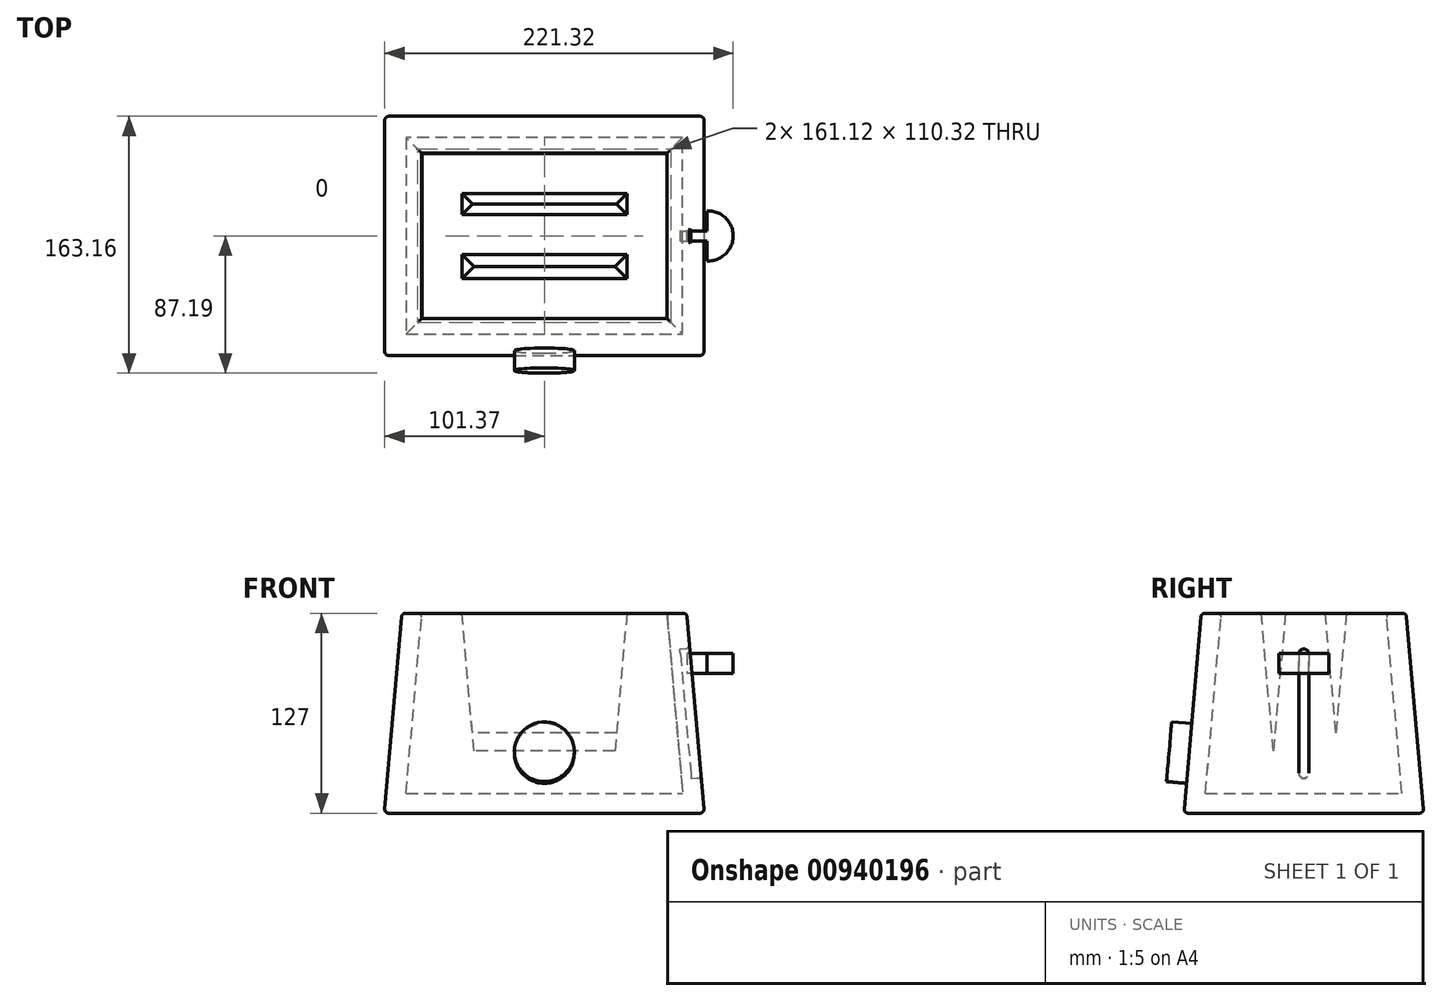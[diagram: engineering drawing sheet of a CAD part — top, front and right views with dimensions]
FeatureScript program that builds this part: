
annotation { "Feature Type Name" : "Feature", "Feature Type Description" : "" }
export const myFeature = defineFeature(function(context is Context, id is Id, definition is map)
    precondition{}
    {
        {
            var Q0;
            Q0=qCreatedBy(makeId("Top.planeOp"),FACE);
            var sketch = newSketch(context, id + "F0", { "sketchPlane" : qUnion([Q0])});
            skLineSegment(sketch, "E0.bottom", {"start": v(101.6, -76.2) * mm, "end": v(-101.6, -76.2) * mm});
            skLineSegment(sketch, "E0.top", {"start": v(101.6, 76.2) * mm, "end": v(-101.6, 76.2) * mm});
            skLineSegment(sketch, "E0.left", {"start": v(101.6, -76.2) * mm, "end": v(101.6, 76.2) * mm});
            skLineSegment(sketch, "E0.right", {"start": v(-101.6, -76.2) * mm, "end": v(-101.6, 76.2) * mm});
            skPoint(sketch, "E0.middle", {"position": v(0, 0) * mm});
            skSolve(sketch);
        }
        {
            var Q0;
            Q0 = qSketchRegion(id + "F0", true);
            extrude(context, id + "F1", {"entities" : qUnion([Q0]), "depth" : 127 * mm, "offsetDistance" : 25.4 * mm, "hasDraft" : true, "draftAngle" : 5 * degree, "draftPullDirection" : true});
        }
        {
            var Q0;
            Q0=makeQuery(id+"F1.opExtrude","CAP_FACE",FACE,{"disambiguationData":[OSD([sQuery(id+"F0.wireOp",EDGE,"E0.bottom"),sQuery(id+"F0.wireOp",EDGE,"E0.top"),sQuery(id+"F0.wireOp",EDGE,"E0.left"),sQuery(id+"F0.wireOp",EDGE,"E0.right")])],"isStart":false});
            var sketch = newSketch(context, id + "F2", { "sketchPlane" : qUnion([Q0])});
            skLineSegment(sketch, "E1.bottom", {"start": v(77.79, -52.39) * mm, "end": v(-77.79, -52.39) * mm});
            skLineSegment(sketch, "E1.top", {"start": v(77.79, 52.39) * mm, "end": v(-77.79, 52.39) * mm});
            skLineSegment(sketch, "E1.left", {"start": v(77.79, -52.39) * mm, "end": v(77.79, 52.39) * mm});
            skLineSegment(sketch, "E1.right", {"start": v(-77.79, -52.39) * mm, "end": v(-77.79, 52.39) * mm});
            skPoint(sketch, "E1.middle", {"position": v(0, 0) * mm});
            skSolve(sketch);
        }
        {
            var Q0;
            Q0=makeQuery(id+"F2.imprint","IMPRINT",FACE,{"disambiguationData":[TD([[makeQuery(id+"F2.imprint","IMPRINT",EDGE,{"derivedFrom":sQuery(id+"F2.wireOp",EDGE,"E1.bottom")}),-1.0]])]});
            extrude(context, id + "F3", {"entities" : qUnion([Q0]), "operationType" : NewBodyOperationType.REMOVE, "oppositeDirection" : true, "depth" : 114.3 * mm, "offsetDistance" : 25.4 * mm, "hasDraft" : true, "draftAngle" : 5 * degree});
        }
        {
            var Q0;
            Q0=makeQuery(id+"F1.opExtrude","CAP_FACE",FACE,{"disambiguationData":[OSD([sQuery(id+"F0.wireOp",EDGE,"E0.bottom"),sQuery(id+"F0.wireOp",EDGE,"E0.top"),sQuery(id+"F0.wireOp",EDGE,"E0.left"),sQuery(id+"F0.wireOp",EDGE,"E0.right")])],"isStart":false});
            var sketch = newSketch(context, id + "F4", { "sketchPlane" : qUnion([Q0])});
            skLineSegment(sketch, "E2.bottom", {"start": v(77.79, -52.39) * mm, "end": v(-77.79, -52.39) * mm});
            skLineSegment(sketch, "E2.top", {"start": v(77.79, 52.39) * mm, "end": v(-77.79, 52.39) * mm});
            skLineSegment(sketch, "E2.left", {"start": v(77.79, -52.39) * mm, "end": v(77.79, 52.39) * mm});
            skLineSegment(sketch, "E2.right", {"start": v(-77.79, -52.39) * mm, "end": v(-77.79, 52.39) * mm});
            skPoint(sketch, "E2.middle", {"position": v(0, 0) * mm});
            skLineSegment(sketch, "E3.bottom", {"start": v(52.39, 13.71) * mm, "end": v(-52.39, 13.71) * mm});
            skLineSegment(sketch, "E3.top", {"start": v(52.39, 26.99) * mm, "end": v(-52.39, 26.99) * mm});
            skLineSegment(sketch, "E3.left", {"start": v(52.39, 13.71) * mm, "end": v(52.39, 26.99) * mm});
            skLineSegment(sketch, "E3.right", {"start": v(-52.39, 13.71) * mm, "end": v(-52.39, 26.99) * mm});
            skPoint(sketch, "E3.middle", {"position": v(0, 20.35) * mm});
            skLineSegment(sketch, "E4.bottom", {"start": v(52.39, -26.99) * mm, "end": v(-52.39, -26.99) * mm});
            skLineSegment(sketch, "E4.top", {"start": v(52.39, -11.69) * mm, "end": v(-52.39, -11.69) * mm});
            skLineSegment(sketch, "E4.left", {"start": v(52.39, -26.99) * mm, "end": v(52.39, -11.69) * mm});
            skLineSegment(sketch, "E4.right", {"start": v(-52.39, -26.99) * mm, "end": v(-52.39, -11.69) * mm});
            skPoint(sketch, "E4.middle", {"position": v(0, -19.34) * mm});
            skSolve(sketch);
        }
        {
            var Q0;
            Q0=makeQuery(id+"F4.imprint","IMPRINT",FACE,{"disambiguationData":[TD([[makeQuery(id+"F4.imprint","IMPRINT",EDGE,{"derivedFrom":sQuery(id+"F4.wireOp",EDGE,"E2.bottom")}),-1.0]])]});
            extrude(context, id + "F5", {"entities" : qUnion([Q0]), "oppositeDirection" : true, "depth" : 114.3 * mm, "offsetDistance" : 25.4 * mm, "hasDraft" : true, "draftAngle" : 5 * degree});
        }
        {
            var Q0;
            Q0=makeQuery(id+"F1.opExtrude","SWEPT_FACE",FACE,{"disambiguationData":[OSD([sQuery(id+"F0.wireOp",EDGE,"E0.bottom")])]});
            var sketch = newSketch(context, id + "F6", { "sketchPlane" : qUnion([Q0])});
            skCircle(sketch, "E5", {"center": v(0, 31.46) * mm, "radius": 19.05 * mm});
            skSolve(sketch);
        }
        {
            var Q0;
            Q0 = qSketchRegion(id + "F6", true);
            extrude(context, id + "F7", {"entities" : qUnion([Q0]), "depth" : 12.7 * mm, "offsetDistance" : 25.4 * mm});
        }
        {
            var Q0;
            Q0=makeQuery(id+"F1.opExtrude","SWEPT_FACE",FACE,{"disambiguationData":[OSD([sQuery(id+"F0.wireOp",EDGE,"E0.left")])]});
            var sketch = newSketch(context, id + "F8", { "sketchPlane" : qUnion([Q0])});
            skLineSegment(sketch, "E6", {"start": v(-3.17, 93.23) * mm, "end": v(-3.18, 17.03) * mm});
            skLineSegment(sketch, "E7", {"start": v(3.17, 93.23) * mm, "end": v(3.18, 17.03) * mm});
            skArc(sketch, "E8", {"start": v(-3.17, 93.23) * mm, "mid": v(0, 96.4) * mm, "end": v(3.17, 93.23) * mm});
            skArc(sketch, "E9", {"start": v(3.18, 17.03) * mm, "mid": v(0, 13.86) * mm, "end": v(-3.18, 17.03) * mm});
            skSolve(sketch);
        }
        {
            var Q0;
            Q0 = qSketchRegion(id + "F8", true);
            extrude(context, id + "F9", {"entities" : qUnion([Q0]), "operationType" : NewBodyOperationType.REMOVE, "oppositeDirection" : true, "depth" : 6.35 * mm, "offsetDistance" : 25.4 * mm});
        }
        {
            var Q0;
            Q0=qCreatedBy(makeId("Top.planeOp"),FACE);
            cPlane(context, id + "F10", {"entities" : qUnion([Q0]), "cplaneType" : CPlaneType.OFFSET, "offset" : 88.9 * mm, "width" : 152.4 * mm, "height" : 152.4 * mm});
        }
        {
            var Q0;
            Q0=qCreatedBy(id+"F10.planeOp",FACE);
            var sketch = newSketch(context, id + "F11", { "sketchPlane" : qUnion([Q0])});
            skLineSegment(sketch, "E10.bottom", {"start": v(103.19, -3.18) * mm, "end": v(90.49, -3.18) * mm});
            skLineSegment(sketch, "E10.top", {"start": v(103.19, 3.17) * mm, "end": v(90.49, 3.17) * mm});
            skLineSegment(sketch, "E10.right", {"start": v(90.49, -3.18) * mm, "end": v(90.49, 3.17) * mm});
            skLineSegment(sketch, "E11", {"start": v(103.19, 3.17) * mm, "end": v(103.19, 15.88) * mm});
            skLineSegment(sketch, "E12", {"start": v(103.19, -3.18) * mm, "end": v(103.19, -15.88) * mm});
            skArc(sketch, "E13", {"start": v(103.19, -15.88) * mm, "mid": v(119.95, 0) * mm, "end": v(103.19, 15.88) * mm});
            skSolve(sketch);
        }
        {
            var Q0;
            Q0 = qSketchRegion(id + "F11", true);
            extrude(context, id + "F12", {"entities" : qUnion([Q0]), "depth" : 12.7 * mm, "offsetDistance" : 25.4 * mm});
        }
        {
            var Q0;
            Q0=makeQuery(id+"F1.opExtrude","CAP_FACE",FACE,{"disambiguationData":[OSD([sQuery(id+"F0.wireOp",EDGE,"E0.bottom"),sQuery(id+"F0.wireOp",EDGE,"E0.top"),sQuery(id+"F0.wireOp",EDGE,"E0.left"),sQuery(id+"F0.wireOp",EDGE,"E0.right")])],"isStart":false});
            var Q1;
            Q1=makeQuery(id+"F1.opExtrude","SWEPT_FACE",FACE,{"disambiguationData":[OSD([sQuery(id+"F0.wireOp",EDGE,"E0.bottom")])]});
            var Q2;
            Q2=makeQuery(id+"F1.opExtrude","SWEPT_FACE",FACE,{"disambiguationData":[OSD([sQuery(id+"F0.wireOp",EDGE,"E0.left")])]});
            var Q3;
            Q3=makeQuery(id+"F1.opExtrude","SWEPT_FACE",FACE,{"disambiguationData":[OSD([sQuery(id+"F0.wireOp",EDGE,"E0.top")])]});
            var Q4;
            Q4=makeQuery(id+"F1.opExtrude","SWEPT_FACE",FACE,{"disambiguationData":[OSD([sQuery(id+"F0.wireOp",EDGE,"E0.right")])]});
            fillet(context, id + "F13", {"entities" : qUnion([Q0, Q1, Q2, Q3, Q4]), "radius" : 2.54 * mm, "tangentPropagation" : true, "allowEdgeOverflow" : false});
        }
    });
